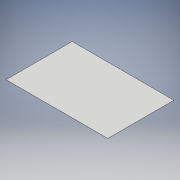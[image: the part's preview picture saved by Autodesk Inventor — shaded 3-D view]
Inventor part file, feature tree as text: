
AUTODESK INVENTOR PART (.ipt)
format: ipt  version: 2017 (Build 210142000, 142)  size: 96,256 bytes
history: native  units: mm
features: sheet_metal_op x1, sketch x1, other x1
ambient origin geometry x8: Origin, YZ Plane, XZ Plane, XY Plane, X Axis, Y Axis, Z Axis, Center Point
bodies: Solid1 (feature_tree)
feature tree (3):
  sheet_metal_op  "Face1"
  sketch  "Sketch1"  dims[d0=400.0mm d1=260.0mm d2=0.5mm]
  other  "Plate1"
